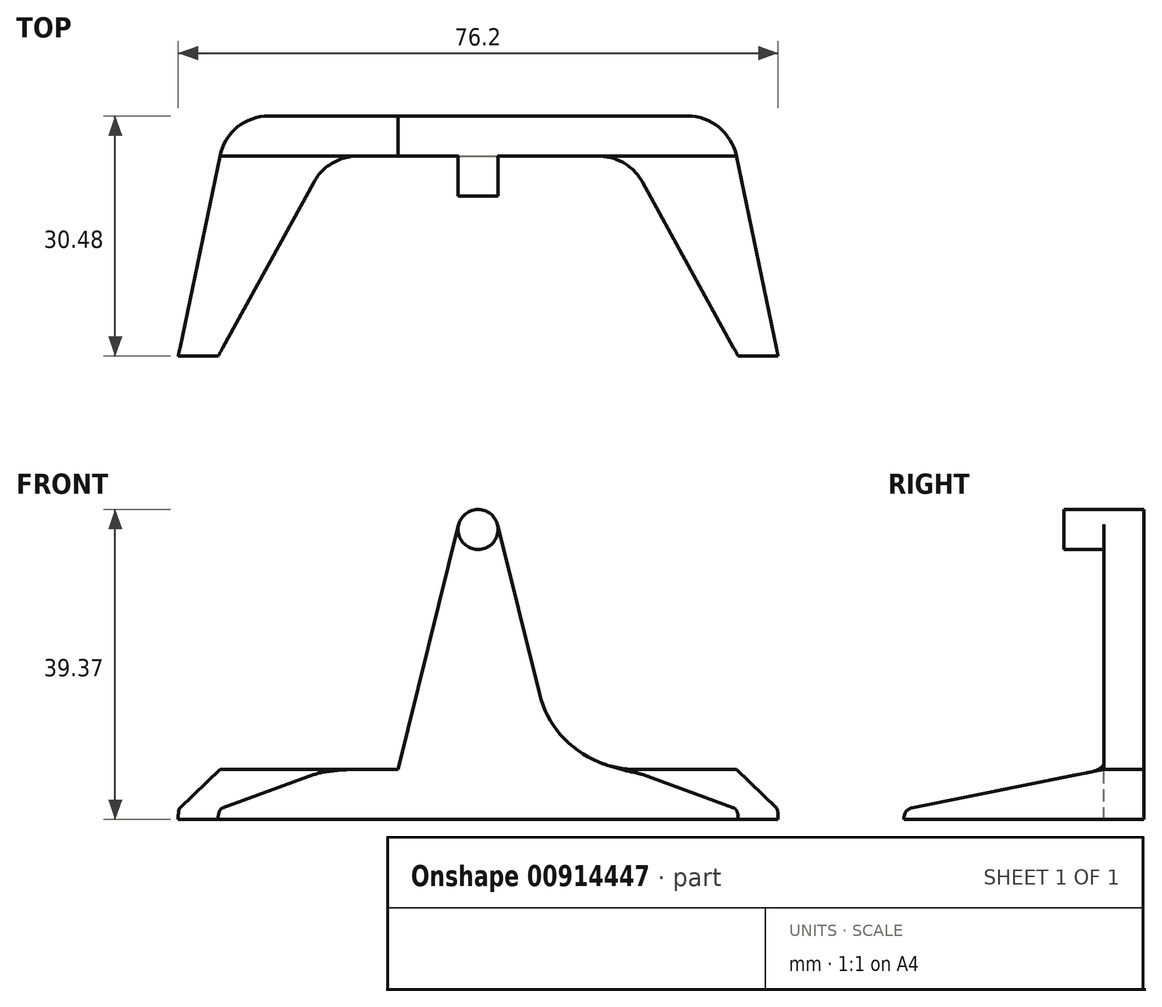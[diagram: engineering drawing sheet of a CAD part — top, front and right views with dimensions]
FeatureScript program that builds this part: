
annotation { "Feature Type Name" : "Feature", "Feature Type Description" : "" }
export const myFeature = defineFeature(function(context is Context, id is Id, definition is map)
    precondition{}
    {
        {
            var Q0;
            Q0=qCreatedBy(makeId("Front.planeOp"),FACE);
            var sketch = newSketch(context, id + "F0", { "sketchPlane" : qUnion([Q0])});
            skArc(sketch, "E0", {"start": v(2.47, 0.61) * mm, "mid": v(0, 2.54) * mm, "end": v(-2.47, 0.61) * mm});
            skLineSegment(sketch, "E1", {"start": v(-10.16, -30.48) * mm, "end": v(-2.47, 0.61) * mm});
            skLineSegment(sketch, "E2", {"start": v(10.16, -30.48) * mm, "end": v(2.47, 0.61) * mm});
            skLineSegment(sketch, "E3", {"start": v(-10.16, -30.48) * mm, "end": v(10.16, -30.48) * mm});
            skSolve(sketch);
        }
        {
            var Q0;
            Q0=makeQuery(id+"F0.imprint","IMPRINT",FACE,{"disambiguationData":[TD([[makeQuery(id+"F0.imprint","IMPRINT",EDGE,{"derivedFrom":sQuery(id+"F0.wireOp",EDGE,"E0")}),1.0]])]});
            extrude(context, id + "F1", {"entities" : qUnion([Q0]), "oppositeDirection" : true, "depth" : 5.08 * mm, "offsetDistance" : 25.4 * mm});
        }
        {
            var Q0;
            Q0=makeQuery(id+"F1.opExtrude","CAP_FACE",FACE,{"disambiguationData":[OSD([sQuery(id+"F0.wireOp",EDGE,"E0"),sQuery(id+"F0.wireOp",EDGE,"E1"),sQuery(id+"F0.wireOp",EDGE,"E2"),sQuery(id+"F0.wireOp",EDGE,"E3")])],"isStart":true});
            var sketch = newSketch(context, id + "F2", { "sketchPlane" : qUnion([Q0])});
            skCircle(sketch, "E4", {"center": v(0, 0) * mm, "radius": 2.54 * mm});
            skPoint(sketch, "E4.first.point", {"position": v(-0.87, 2.39) * mm});
            skPoint(sketch, "E4.second.point", {"position": v(-1.95, 1.63) * mm});
            skPoint(sketch, "E4.third.point", {"position": v(0.92, 2.37) * mm});
            skSolve(sketch);
        }
        {
            var Q0;
            {var subQ0=sQuery(id+"F2.wireOp",EDGE,"E4");var subQ1=makeQuery(id+"F2.imprint","INTERSECT",VERTEX,{"derivedFrom":[makeQuery(id+"F1.opExtrude","CAP_EDGE",EDGE,{"disambiguationData":[OSD([sQuery(id+"F0.wireOp",EDGE,"E2")])],"isStart":true}),subQ0]});Q0=makeQuery(id+"F2.imprint","IMPRINT",FACE,{"disambiguationData":[TD([[makeQuery(id+"F2.imprint","IMPRINT",EDGE,{"disambiguationData":[TD([[subQ1,-1.0]])],"derivedFrom":subQ0}),1.0]])]});}
            extrude(context, id + "F3", {"entities" : qUnion([Q0]), "operationType" : NewBodyOperationType.ADD, "depth" : 5.08 * mm, "offsetDistance" : 25.4 * mm});
        }
        {
            var Q0;
            Q0=makeQuery(id+"F1.opExtrude","SWEPT_FACE",FACE,{"disambiguationData":[OSD([sQuery(id+"F0.wireOp",EDGE,"E3")])]});
            var sketch = newSketch(context, id + "F4", { "sketchPlane" : qUnion([Q0])});
            skLineSegment(sketch, "E5.bottom", {"start": v(-26.59, -5.08) * mm, "end": v(26.59, -5.08) * mm});
            skLineSegment(sketch, "E6", {"start": v(-38.1, 25.4) * mm, "end": v(-33.02, 25.4) * mm});
            skLineSegment(sketch, "E7", {"start": v(-33.02, 25.4) * mm, "end": v(-20.86, 3.29) * mm});
            skLineSegment(sketch, "E8", {"start": v(20.86, 3.29) * mm, "end": v(33.02, 25.4) * mm});
            skLineSegment(sketch, "E9", {"start": v(33.02, 25.4) * mm, "end": v(38.1, 25.4) * mm});
            skLineSegment(sketch, "E10", {"start": v(-15.3, 0) * mm, "end": v(15.3, 0) * mm});
            skPoint(sketch, "E11.visualSharp", {"position": v(-19.05, 0) * mm});
            skArc(sketch, "E11.filletArc", {"start": v(-20.86, 3.29) * mm, "mid": v(-18.53, 0.88) * mm, "end": v(-15.3, 0) * mm});
            skPoint(sketch, "E12.visualSharp", {"position": v(19.05, 0) * mm});
            skArc(sketch, "E12.filletArc", {"start": v(15.3, 0) * mm, "mid": v(18.53, 0.88) * mm, "end": v(20.86, 3.29) * mm});
            skLineSegment(sketch, "E13", {"start": v(-15.3, 0) * mm, "end": v(0, 0) * mm});
            skLineSegment(sketch, "E14", {"start": v(-38.1, 25.4) * mm, "end": v(-32.8, -0.03) * mm});
            skLineSegment(sketch, "E15", {"start": v(38.1, 25.4) * mm, "end": v(32.8, -0.03) * mm});
            skPoint(sketch, "E16.visualSharp", {"position": v(-31.75, -5.08) * mm});
            skArc(sketch, "E16.filletArc", {"start": v(-32.8, -0.03) * mm, "mid": v(-30.6, -3.66) * mm, "end": v(-26.59, -5.08) * mm});
            skPoint(sketch, "E17.visualSharp", {"position": v(31.75, -5.08) * mm});
            skArc(sketch, "E17.filletArc", {"start": v(26.59, -5.08) * mm, "mid": v(30.6, -3.66) * mm, "end": v(32.8, -0.03) * mm});
            skSolve(sketch);
        }
        {
            var Q0;
            Q0=makeQuery(id+"F4.imprint","IMPRINT",FACE,{"disambiguationData":[TD([[makeQuery(id+"F4.imprint","IMPRINT",EDGE,{"derivedFrom":sQuery(id+"F4.wireOp",EDGE,"E6")}),-1.0]])]});
            var Q1;
            {var subQ0=sQuery(id+"F0.wireOp",EDGE,"E3");var subQ1=makeQuery(id+"F1.opExtrude","SWEPT_EDGE",EDGE,{"disambiguationData":[OSD([sQuery(id+"F0.wireOp",EDGE,"E1"),subQ0])]});Q1=makeQuery(id+"F4.imprint","IMPRINT",FACE,{"disambiguationData":[TD([[makeQuery(id+"F4.imprint","IMPRINT",EDGE,{"derivedFrom":subQ1}),-1.0]])]});}
            var Q2;
            Q2=makeQuery(id+"F4.imprint","IMPRINT",FACE,{"disambiguationData":[TD([[makeQuery(id+"F4.imprint","IMPRINT",EDGE,{"derivedFrom":sQuery(id+"F4.wireOp",EDGE,"E8")}),-1.0]])]});
            extrude(context, id + "F5", {"entities" : qUnion([Q0, Q1, Q2]), "operationType" : NewBodyOperationType.ADD, "depth" : 6.35 * mm, "offsetDistance" : 25.4 * mm});
        }
        {
            var Q0;
            Q0=makeQuery(id+"F1.opExtrude","SWEPT_EDGE",EDGE,{"disambiguationData":[OSD([sQuery(id+"F0.wireOp",EDGE,"E2"),sQuery(id+"F0.wireOp",EDGE,"E3")])]});
            var Q1;
            Q1=makeQuery(id+"F1.opExtrude","SWEPT_EDGE",EDGE,{"disambiguationData":[OSD([sQuery(id+"F0.wireOp",EDGE,"E1"),sQuery(id+"F0.wireOp",EDGE,"E3")])]});
            fillet(context, id + "F6", {"entities" : qUnion([Q0, Q1]), "radius" : 12.7 * mm, "tangentPropagation" : true, "allowEdgeOverflow" : false});
        }
        {
            var Q0;
            Q0=makeQuery(id+"F5.opExtrude","CAP_EDGE",EDGE,{"disambiguationData":[OSD([sQuery(id+"F4.wireOp",EDGE,"E6")])],"isStart":true});
            var Q1;
            Q1=makeQuery(id+"F5.opExtrude","CAP_EDGE",EDGE,{"disambiguationData":[OSD([sQuery(id+"F4.wireOp",EDGE,"E9")])],"isStart":true});
            chamfer(context, id + "F7", {"entities" : qUnion([Q0, Q1]), "chamferType" : ChamferType.TWO_OFFSETS, "width1" : 25.4 * mm, "oppositeDirection" : false, "width2" : 5.08 * mm, "tangentPropagation" : true});
        }
        {
            var Q0;
            {var subQ0=sQuery(id+"F4.wireOp",EDGE,"E6");Q0=makeQuery(id+"F7.opChamfer","BLEND_EDGE",EDGE,{"blendedFrom":[makeQuery(id+"F5.opExtrude","CAP_EDGE",EDGE,{"disambiguationData":[OSD([subQ0])],"isStart":true}),makeQuery(id+"F5.opExtrude","SWEPT_FACE",FACE,{"disambiguationData":[OSD([subQ0])]})],"blendedInto":[makeQuery(id+"F5.opExtrude","SWEPT_FACE",FACE,{"disambiguationData":[OSD([subQ0])]})]});}
            var Q1;
            {var subQ0=sQuery(id+"F4.wireOp",EDGE,"E9");Q1=makeQuery(id+"F7.opChamfer","BLEND_EDGE",EDGE,{"blendedFrom":[makeQuery(id+"F5.opExtrude","CAP_EDGE",EDGE,{"disambiguationData":[OSD([subQ0])],"isStart":true}),makeQuery(id+"F5.opExtrude","SWEPT_FACE",FACE,{"disambiguationData":[OSD([subQ0])]})],"blendedInto":[makeQuery(id+"F5.opExtrude","SWEPT_FACE",FACE,{"disambiguationData":[OSD([subQ0])]})]});}
            fillet(context, id + "F8", {"entities" : qUnion([Q0, Q1]), "radius" : 1.27 * mm, "tangentPropagation" : true, "allowEdgeOverflow" : false});
        }
    });
